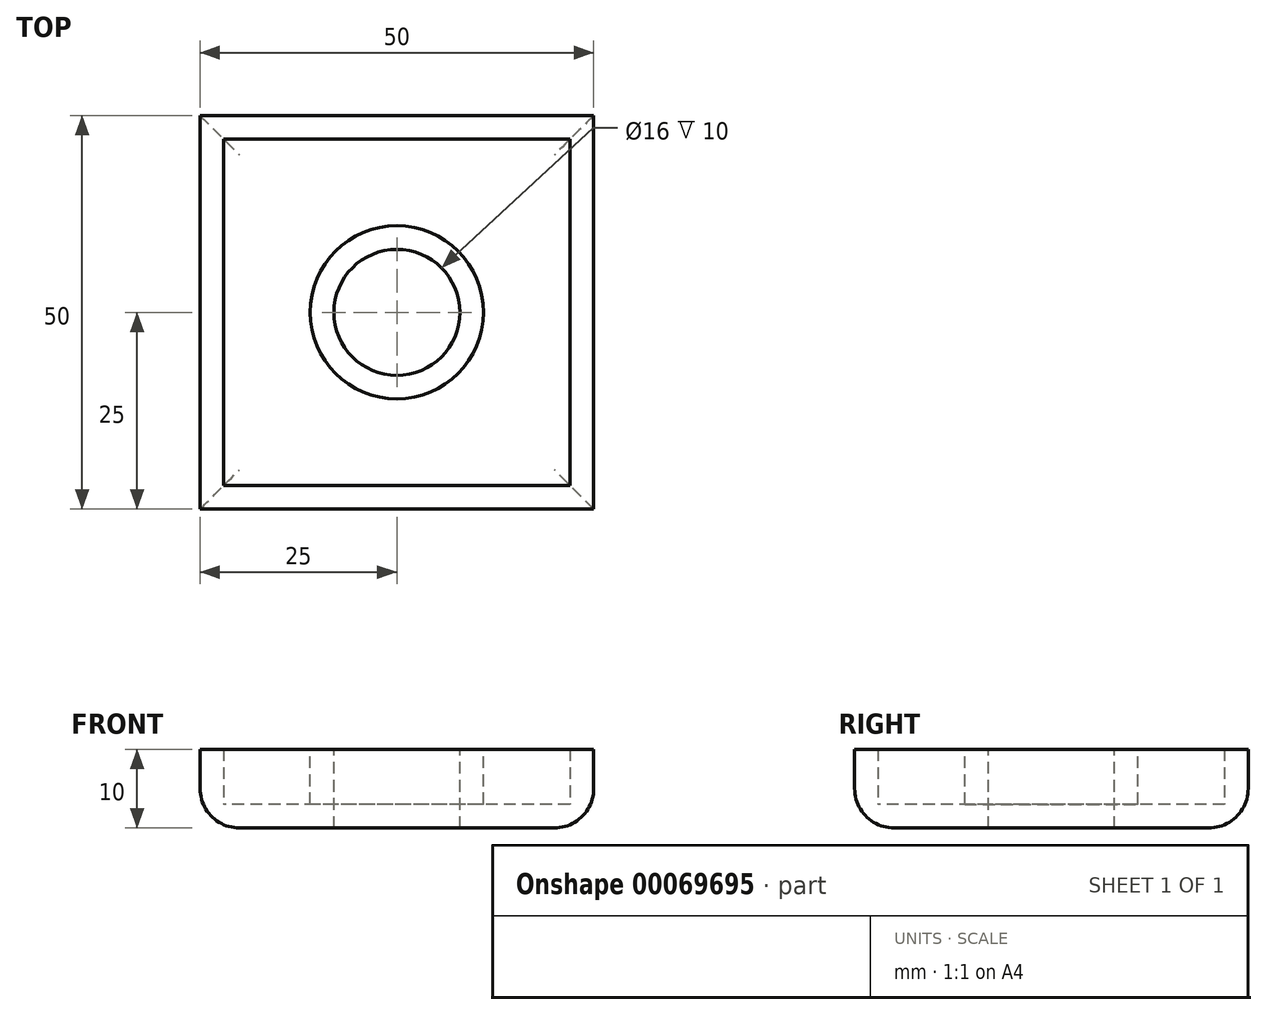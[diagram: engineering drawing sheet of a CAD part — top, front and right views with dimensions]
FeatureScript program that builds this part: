
annotation { "Feature Type Name" : "Feature", "Feature Type Description" : "" }
export const myFeature = defineFeature(function(context is Context, id is Id, definition is map)
    precondition{}
    {
        {
            var Q0;
            Q0=qCreatedBy(makeId("Top.planeOp"),FACE);
            var sketch = newSketch(context, id + "F0", { "sketchPlane" : qUnion([Q0])});
            skLineSegment(sketch, "E0.rect.bottom", {"start": v(25, 25) * mm, "end": v(-25, 25) * mm});
            skLineSegment(sketch, "E0.rect.top", {"start": v(25, -25) * mm, "end": v(-25, -25) * mm});
            skLineSegment(sketch, "E0.rect.left", {"start": v(25, 25) * mm, "end": v(25, -25) * mm});
            skLineSegment(sketch, "E0.rect.right", {"start": v(-25, 25) * mm, "end": v(-25, -25) * mm});
            skPoint(sketch, "E0.rect.middle", {"position": v(0, 0) * mm});
            skSolve(sketch);
        }
        {
            var Q0;
            Q0=makeQuery(id+"F0.imprint","IMPRINT",FACE,{"disambiguationData":[TD([[makeQuery(id+"F0.imprint","IMPRINT",EDGE,{"derivedFrom":sQuery(id+"F0.wireOp",EDGE,"E0.rect.bottom")}),1.0]])]});
            extrude(context, id + "F1", {"entities" : qUnion([Q0]), "depth" : 10 * mm});
        }
        {
            var Q0;
            Q0=makeQuery(id+"F1.opExtrude","CAP_FACE",FACE,{"disambiguationData":[OSD([sQuery(id+"F0.wireOp",EDGE,"E0.rect.bottom"),sQuery(id+"F0.wireOp",EDGE,"E0.rect.top"),sQuery(id+"F0.wireOp",EDGE,"E0.rect.left"),sQuery(id+"F0.wireOp",EDGE,"E0.rect.right")])],"isStart":false});
            var sketch = newSketch(context, id + "F2", { "sketchPlane" : qUnion([Q0])});
            skSolve(sketch);
        }
        {
            var Q0;
            Q0=makeQuery(id+"F2.imprint","IMPRINT",FACE,{"disambiguationData":[TD([[makeQuery(id+"F2.imprint","IMPRINT",EDGE,{"derivedFrom":makeQuery(id+"F1.opExtrude","CAP_EDGE",EDGE,{"disambiguationData":[OSD([sQuery(id+"F0.wireOp",EDGE,"E0.rect.bottom")])],"isStart":false})}),1.0]])]});
            var sketch = newSketch(context, id + "F3", { "sketchPlane" : qUnion([Q0])});
            skPoint(sketch, "E1", {"position": v(0, 0) * mm});
            skSolve(sketch);
        }
        {
            var Q0;
            Q0=sQuery(id+"F3.wireOp",VERTEX,"E1");
            var Q1;
            Q1=makeQuery(id+"F1.opExtrude","SWEPT_BODY",BODY,{"disambiguationData":[OSD([sQuery(id+"F0.wireOp",EDGE,"E0.rect.bottom"),sQuery(id+"F0.wireOp",EDGE,"E0.rect.top"),sQuery(id+"F0.wireOp",EDGE,"E0.rect.left"),sQuery(id+"F0.wireOp",EDGE,"E0.rect.right")])]});
            hole(context, id + "F4", {"style" : HoleStyle.SIMPLE, "holeDiameter" : 16 * mm, "endStyle" : HoleEndStyle.THROUGH, "locations" : qUnion([Q0]), "scope" : qUnion([Q1]), "isTappedThrough" : true});
        }
        {
            var Q0;
            Q0=makeQuery(id+"F1.opExtrude","CAP_FACE",FACE,{"disambiguationData":[OSD([sQuery(id+"F0.wireOp",EDGE,"E0.rect.bottom"),sQuery(id+"F0.wireOp",EDGE,"E0.rect.top"),sQuery(id+"F0.wireOp",EDGE,"E0.rect.left"),sQuery(id+"F0.wireOp",EDGE,"E0.rect.right")])],"isStart":false});
            shell(context, id + "F5", {"entities" : qUnion([Q0]), "thickness" : 3 * mm});
        }
        {
            var Q0;
            Q0=makeQuery(id+"F1.opExtrude","CAP_EDGE",EDGE,{"disambiguationData":[OSD([sQuery(id+"F0.wireOp",EDGE,"E0.rect.right")])],"isStart":true});
            var Q1;
            Q1=makeQuery(id+"F1.opExtrude","CAP_EDGE",EDGE,{"disambiguationData":[OSD([sQuery(id+"F0.wireOp",EDGE,"E0.rect.bottom")])],"isStart":true});
            var Q2;
            Q2=makeQuery(id+"F1.opExtrude","CAP_EDGE",EDGE,{"disambiguationData":[OSD([sQuery(id+"F0.wireOp",EDGE,"E0.rect.left")])],"isStart":true});
            var Q3;
            Q3=makeQuery(id+"F1.opExtrude","CAP_EDGE",EDGE,{"disambiguationData":[OSD([sQuery(id+"F0.wireOp",EDGE,"E0.rect.top")])],"isStart":true});
            fillet(context, id + "F6", {"entities" : qUnion([Q0, Q1, Q2, Q3]), "radius" : 5 * mm, "tangentPropagation" : true, "allowEdgeOverflow" : false});
        }
    });
